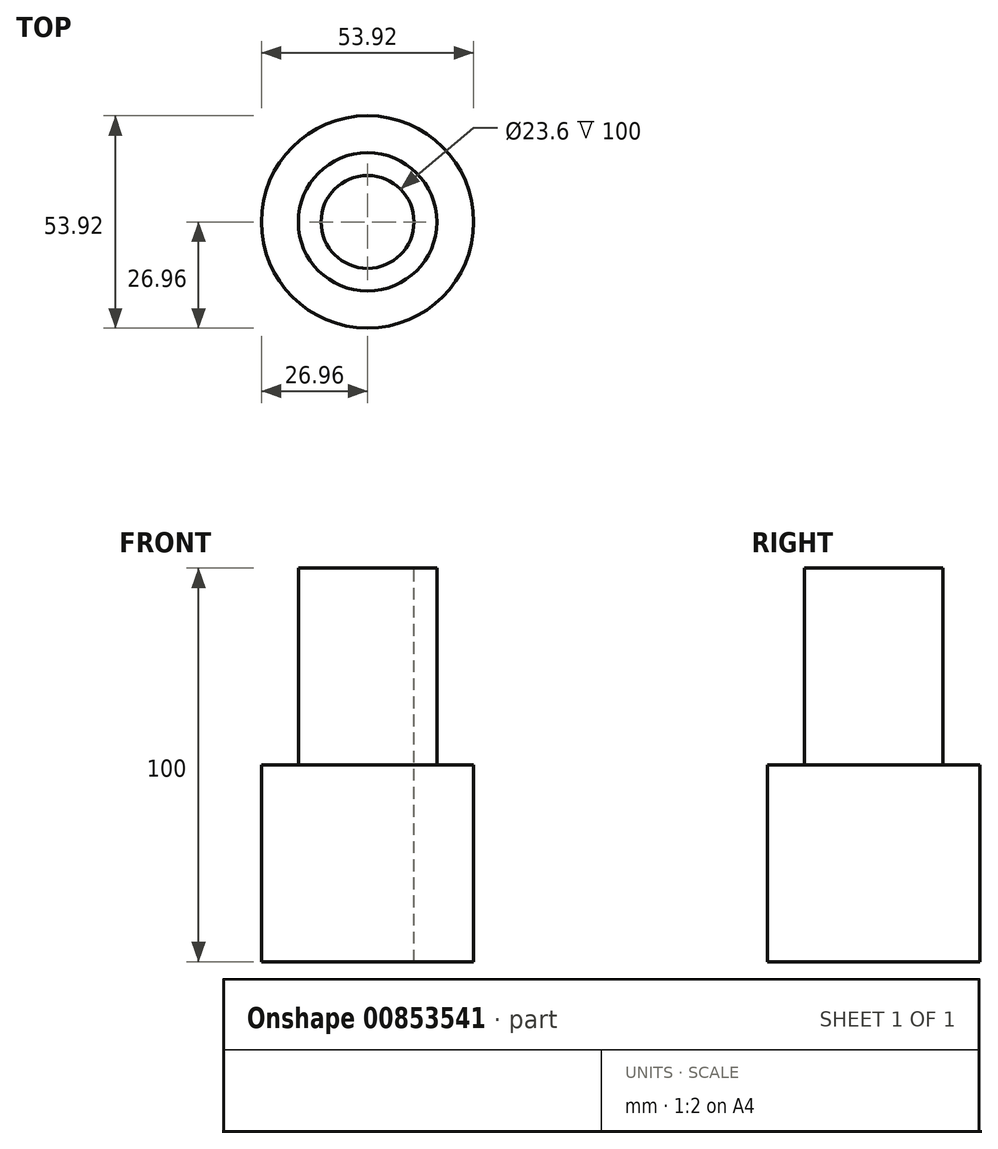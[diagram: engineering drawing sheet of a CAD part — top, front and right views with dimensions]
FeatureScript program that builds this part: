
annotation { "Feature Type Name" : "Feature", "Feature Type Description" : "" }
export const myFeature = defineFeature(function(context is Context, id is Id, definition is map)
    precondition{}
    {
        {
            var Q0;
            Q0=qCreatedBy(makeId("Top.planeOp"),FACE);
            var sketch = newSketch(context, id + "F0", { "sketchPlane" : qUnion([Q0])});
            skCircle(sketch, "E0", {"center": v(0, 0) * mm, "radius": 26.96 * mm});
            skSolve(sketch);
        }
        {
            var Q0;
            Q0 = qSketchRegion(id + "F0", true);
            extrude(context, id + "F1", {"entities" : qUnion([Q0]), "depth" : 50 * mm, "offsetDistance" : 25 * mm});
        }
        {
            var Q0;
            Q0=makeQuery(id+"F1.opExtrude","CAP_FACE",FACE,{"disambiguationData":[OSD([sQuery(id+"F0.wireOp",EDGE,"E0")])],"isStart":false});
            var sketch = newSketch(context, id + "F2", { "sketchPlane" : qUnion([Q0])});
            skCircle(sketch, "E1", {"center": v(0, 0) * mm, "radius": 17.58 * mm});
            skSolve(sketch);
        }
        {
            var Q0;
            Q0 = qSketchRegion(id + "F2", true);
            extrude(context, id + "F3", {"entities" : qUnion([Q0]), "operationType" : NewBodyOperationType.ADD, "depth" : 50 * mm, "offsetDistance" : 25 * mm});
        }
        {
            var Q0;
            Q0=makeQuery(id+"F3.opExtrude","CAP_FACE",FACE,{"disambiguationData":[OSD([sQuery(id+"F2.wireOp",EDGE,"E1")])],"isStart":false});
            var sketch = newSketch(context, id + "F4", { "sketchPlane" : qUnion([Q0])});
            skCircle(sketch, "E2", {"center": v(0, 0) * mm, "radius": 11.8 * mm});
            skSolve(sketch);
        }
        {
            var Q0;
            Q0 = qSketchRegion(id + "F4", true);
            extrude(context, id + "F5", {"entities" : qUnion([Q0]), "operationType" : NewBodyOperationType.REMOVE, "endBound" : BoundingType.THROUGH_ALL, "oppositeDirection" : true, "depth" : 25 * mm, "offsetDistance" : 25 * mm});
        }
    });
